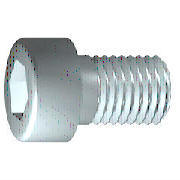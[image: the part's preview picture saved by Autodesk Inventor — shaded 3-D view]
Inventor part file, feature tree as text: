
AUTODESK INVENTOR PART (.ipt)
format: ipt  version: 2024 (Build 280153000, 153)  size: 189,952 bytes
history: native  units: mm (DEFAULTED — no unit token found)
features: fillet x2, sketch x2, extrude x1, thread x1, chamfer x1, plane x1
ambient origin geometry x7: Origin, YZ Plane, XY Plane, X Axis, Y Axis, Z Axis, Center Point
bodies: Solid1 (feature_tree), Body (feature_tree)
feature tree (8):
  extrude  "Slot"  Depth=2.0mm
  fillet  "Fillet1"  Radius=4.0mm
  thread  "Thread"  [1 undecoded]
  chamfer  "Chamfer1"  Distance=4.0mm
  plane  "Work Plane1"
  fillet  "Fillet2"  Radius=4.0mm
  sketch  "Sketch1"  dims[d1=14.25mm d2=0.429515mm d3=4.0mm d4=2.0mm]
  sketch  "Sketch2"  dims[d5=60.0deg d6=4.0mm d7=4.0mm d8=3.464102mm d9=7.0mm d10=90.0deg d11=10.0mm d12=0.0mm d13=14.25mm d14=0.0mm d15=0.429415mm d16=0.429415mm d17=0.4mm d19=0.0mm d26=16.0mm d27=45.0deg d28=0.0mm d29=0.0mm d30=0.1mm]
note: 1 required parameter value undecoded (feature->parameter linkage not recoverable at this tier; creation-order binding heuristic only, values carry confidence <= 0.55)
